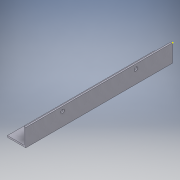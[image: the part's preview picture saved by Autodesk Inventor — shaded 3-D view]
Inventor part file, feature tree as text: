
AUTODESK INVENTOR PART (.ipt)
format: ipt  version: 2019 (Build 230136000, 136)  size: 106,496 bytes
history: native  units: in
note: dims shown in document units (in); Inventor stores cm internally (conversion verified against a paired STEP export)
features: sketch x3, extrude x2
ambient origin geometry x8: Origin, YZ Plane, XZ Plane, XY Plane, X Axis, Y Axis, Z Axis, Center Point
bodies: Solid1 (feature_tree)
feature tree (5):
  extrude  "Extrusion1"  TaperAngle=0.0deg  [1 undecoded]
  extrude  "Extrusion2"  [1 undecoded]
  sketch  "Sketch3"
  sketch  "Sketch1"  dims[d4=7.874in d5=0.0in d12=0.0in d13=0.0in]
  sketch  "Sketch2"
note: 2 required parameter values undecoded (feature->parameter linkage not recoverable at this tier; creation-order binding heuristic only, values carry confidence <= 0.55)
